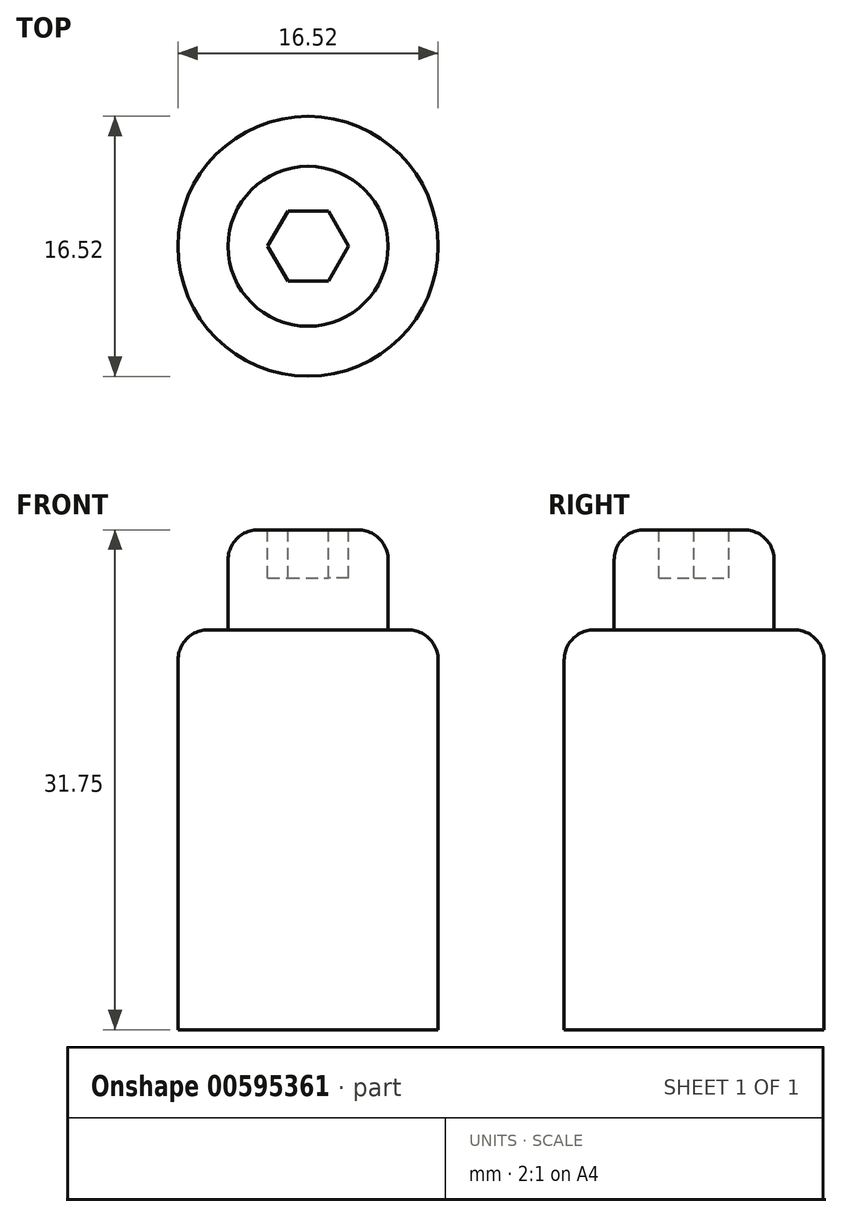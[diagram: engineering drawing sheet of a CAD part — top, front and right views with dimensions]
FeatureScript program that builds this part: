
annotation { "Feature Type Name" : "Feature", "Feature Type Description" : "" }
export const myFeature = defineFeature(function(context is Context, id is Id, definition is map)
    precondition{}
    {
        {
            var Q0;
            Q0=qCreatedBy(makeId("Top.planeOp"),FACE);
            var sketch = newSketch(context, id + "F0", { "sketchPlane" : qUnion([Q0])});
            skCircle(sketch, "E0", {"center": v(0, 0) * mm, "radius": 8.26 * mm});
            skSolve(sketch);
        }
        {
            var Q0;
            Q0 = qSketchRegion(id + "F0", true);
            extrude(context, id + "F1", {"entities" : qUnion([Q0]), "depth" : 25.4 * mm, "offsetDistance" : 25.4 * mm});
        }
        {
            var Q0;
            Q0=makeQuery(id+"F1.opExtrude","CAP_FACE",FACE,{"disambiguationData":[OSD([sQuery(id+"F0.wireOp",EDGE,"E0")])],"isStart":false});
            var sketch = newSketch(context, id + "F2", { "sketchPlane" : qUnion([Q0])});
            skCircle(sketch, "E1", {"center": v(0, 0) * mm, "radius": 5.08 * mm});
            skSolve(sketch);
        }
        {
            var Q0;
            Q0 = qSketchRegion(id + "F2", true);
            extrude(context, id + "F3", {"entities" : qUnion([Q0]), "operationType" : NewBodyOperationType.ADD, "depth" : 6.35 * mm, "offsetDistance" : 25.4 * mm});
        }
        {
            var Q0;
            Q0=makeQuery(id+"F3.opExtrude","CAP_FACE",FACE,{"disambiguationData":[OSD([sQuery(id+"F2.wireOp",EDGE,"E1")])],"isStart":false});
            var sketch = newSketch(context, id + "F4", { "sketchPlane" : qUnion([Q0])});
            skCircle(sketch, "E2.cCircle", {"center": v(0, 0) * mm, "radius": 2.22 * mm, "construction": true});
            skLineSegment(sketch, "E2.0", {"start": v(-1.28, 2.22) * mm, "end": v(1.28, 2.22) * mm});
            skLineSegment(sketch, "E2.1", {"start": v(1.28, 2.22) * mm, "end": v(2.57, 0) * mm});
            skLineSegment(sketch, "E2.2", {"start": v(2.57, 0) * mm, "end": v(1.28, -2.22) * mm});
            skLineSegment(sketch, "E2.3", {"start": v(1.28, -2.22) * mm, "end": v(-1.28, -2.22) * mm});
            skLineSegment(sketch, "E2.4", {"start": v(-1.28, -2.22) * mm, "end": v(-2.57, 0) * mm});
            skLineSegment(sketch, "E2.5", {"start": v(-2.57, 0) * mm, "end": v(-1.28, 2.22) * mm});
            skPoint(sketch, "E2.0.midPoint", {"position": v(0, 2.22) * mm});
            skSolve(sketch);
        }
        {
            var Q0;
            Q0 = qSketchRegion(id + "F4", true);
            extrude(context, id + "F5", {"entities" : qUnion([Q0]), "operationType" : NewBodyOperationType.REMOVE, "oppositeDirection" : true, "depth" : 3.05 * mm, "offsetDistance" : 25.4 * mm});
        }
        {
            var Q0;
            Q0=makeQuery(id+"F1.opExtrude","CAP_EDGE",EDGE,{"disambiguationData":[OSD([sQuery(id+"F0.wireOp",EDGE,"E0")])],"isStart":false});
            var Q1;
            Q1=makeQuery(id+"F3.opExtrude","CAP_EDGE",EDGE,{"disambiguationData":[OSD([sQuery(id+"F2.wireOp",EDGE,"E1")])],"isStart":false});
            fillet(context, id + "F6", {"entities" : qUnion([Q0, Q1]), "radius" : 1.9 * mm, "tangentPropagation" : true, "allowEdgeOverflow" : false});
        }
    });
